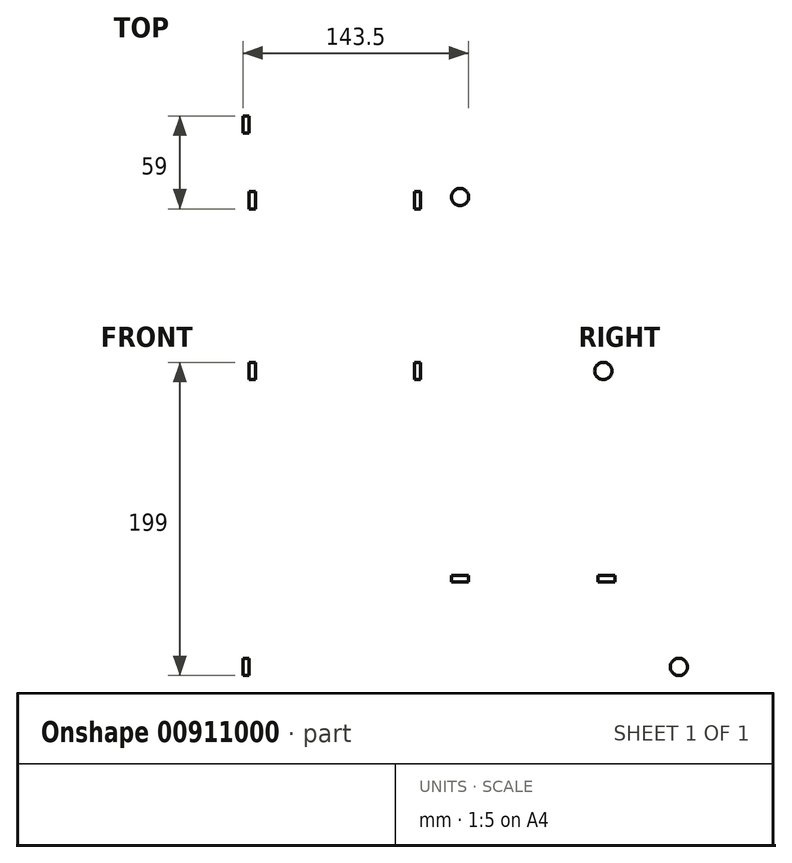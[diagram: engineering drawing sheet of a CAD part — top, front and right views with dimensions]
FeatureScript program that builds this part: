
annotation { "Feature Type Name" : "Feature", "Feature Type Description" : "" }
export const myFeature = defineFeature(function(context is Context, id is Id, definition is map)
    precondition{}
    {
        {
            var Q0;
            Q0=qCreatedBy(makeId("Front.planeOp"),FACE);
            var sketch = newSketch(context, id + "F0", { "sketchPlane" : qUnion([Q0])});
            skLineSegment(sketch, "E0", {"start": v(0, 0) * mm, "end": v(150, 0) * mm});
            skLineSegment(sketch, "E1", {"start": v(0, 0) * mm, "end": v(0, -70) * mm});
            skLineSegment(sketch, "E2.0", {"start": v(-4, 4) * mm, "end": v(-4, -70) * mm});
            skLineSegment(sketch, "E2.1", {"start": v(-4, 4) * mm, "end": v(150, 4) * mm});
            skLineSegment(sketch, "E3", {"start": v(-4, -70) * mm, "end": v(0, -70) * mm});
            skLineSegment(sketch, "E4", {"start": v(150, 0) * mm, "end": v(150, 4) * mm});
            skSolve(sketch);
        }
        {
            var Q0;
            Q0=makeQuery(id+"F0.imprint","IMPRINT",FACE,{"disambiguationData":[TD([[makeQuery(id+"F0.imprint","IMPRINT",EDGE,{"derivedFrom":sQuery(id+"F0.wireOp",EDGE,"E0")}),1.0]])]});
            var sketch = newSketch(context, id + "F1", { "sketchPlane" : qUnion([Q0])});
            skLineSegment(sketch, "E5", {"start": v(105, 4) * mm, "end": v(105, 204) * mm});
            skLineSegment(sketch, "E6", {"start": v(4, 83) * mm, "end": v(105, 83) * mm});
            skLineSegment(sketch, "E7.0", {"start": v(0, 4) * mm, "end": v(0, 204) * mm});
            skLineSegment(sketch, "E8.0", {"start": v(109, 4) * mm, "end": v(109, 204) * mm});
            skLineSegment(sketch, "E9.0", {"start": v(4, 79) * mm, "end": v(105, 79) * mm});
            skLineSegment(sketch, "E10", {"start": v(109, 4) * mm, "end": v(105, 4) * mm});
            skLineSegment(sketch, "E11", {"start": v(0, 4) * mm, "end": v(4, 4) * mm});
            skLineSegment(sketch, "E12", {"start": v(4, 4) * mm, "end": v(4, 204) * mm});
            skLineSegment(sketch, "E13", {"start": v(4, 204) * mm, "end": v(0, 204) * mm});
            skLineSegment(sketch, "E14", {"start": v(109, 204) * mm, "end": v(105, 204) * mm});
            skSolve(sketch);
        }
        {
            var Q0;
            Q0=makeQuery(id+"F0.imprint","IMPRINT",FACE,{"disambiguationData":[TD([[makeQuery(id+"F0.imprint","IMPRINT",EDGE,{"derivedFrom":sQuery(id+"F0.wireOp",EDGE,"E0")}),1.0]])]});
            var Q1;
            Q1=makeQuery(id+"F1.imprint","IMPRINT",FACE,{"disambiguationData":[TD([[makeQuery(id+"F1.imprint","IMPRINT",EDGE,{"derivedFrom":sQuery(id+"F1.wireOp",EDGE,"E7.0")}),-1.0]])]});
            var Q2;
            {var subQ0=sQuery(id+"F1.wireOp",EDGE,"E6");Q2=makeQuery(id+"F1.imprint","IMPRINT",FACE,{"disambiguationData":[TD([[makeQuery(id+"F1.imprint","IMPRINT",EDGE,{"derivedFrom":subQ0}),-1.0]])]});}
            var Q3;
            Q3=makeQuery(id+"F1.imprint","IMPRINT",FACE,{"disambiguationData":[TD([[makeQuery(id+"F1.imprint","IMPRINT",EDGE,{"derivedFrom":sQuery(id+"F1.wireOp",EDGE,"E8.0")}),1.0]])]});
            extrude(context, id + "F2", {"entities" : qUnion([Q0, Q1, Q2, Q3]), "depth" : 80 * mm, "offsetDistance" : 25 * mm});
        }
        {
            var Q0;
            Q0=makeQuery(id+"F2.opExtrude","SWEPT_FACE",FACE,{"disambiguationData":[OSD([sQuery(id+"F0.wireOp",EDGE,"E2.1")])]});
            var sketch = newSketch(context, id + "F3", { "sketchPlane" : qUnion([Q0])});
            skLineSegment(sketch, "E15", {"start": v(150, -40) * mm, "end": v(105.86, -40) * mm, "construction": true});
            skCircle(sketch, "E16", {"center": v(134, -17) * mm, "radius": 5.5 * mm});
            skCircle(sketch, "E17.MirrorC", {"center": v(134, -63) * mm, "radius": 5.5 * mm});
            skSolve(sketch);
        }
        {
            var Q0;
            Q0=makeQuery(id+"F2.opExtrude","SWEPT_FACE",FACE,{"disambiguationData":[OSD([sQuery(id+"F0.wireOp",EDGE,"E2.0")])]});
            var sketch = newSketch(context, id + "F4", { "sketchPlane" : qUnion([Q0])});
            skCircle(sketch, "E18", {"center": v(63, -54) * mm, "radius": 5.5 * mm});
            skLineSegment(sketch, "E19", {"start": v(40, -70) * mm, "end": v(40, -26.92) * mm, "construction": true});
            skCircle(sketch, "E20.MirrorC", {"center": v(17, -54) * mm, "radius": 5.5 * mm});
            skSolve(sketch);
        }
        {
            var Q0;
            Q0=makeQuery(id+"F3.imprint","IMPRINT",FACE,{"disambiguationData":[TD([[makeQuery(id+"F3.imprint","IMPRINT",EDGE,{"derivedFrom":sQuery(id+"F3.wireOp",EDGE,"E16")}),1.0]])]});
            var Q1;
            Q1=makeQuery(id+"F3.imprint","IMPRINT",FACE,{"disambiguationData":[TD([[makeQuery(id+"F3.imprint","IMPRINT",EDGE,{"derivedFrom":sQuery(id+"F3.wireOp",EDGE,"E17.MirrorC")}),-1.0]])]});
            extrude(context, id + "F5", {"entities" : qUnion([Q0, Q1]), "operationType" : NewBodyOperationType.REMOVE, "oppositeDirection" : true, "depth" : 25 * mm, "offsetDistance" : 25 * mm});
        }
        {
            var Q0;
            Q0=makeQuery(id+"F4.imprint","IMPRINT",FACE,{"disambiguationData":[TD([[makeQuery(id+"F4.imprint","IMPRINT",EDGE,{"derivedFrom":sQuery(id+"F4.wireOp",EDGE,"E20.MirrorC")}),-1.0]])]});
            var Q1;
            Q1=makeQuery(id+"F4.imprint","IMPRINT",FACE,{"disambiguationData":[TD([[makeQuery(id+"F4.imprint","IMPRINT",EDGE,{"derivedFrom":sQuery(id+"F4.wireOp",EDGE,"E18")}),1.0]])]});
            extrude(context, id + "F6", {"entities" : qUnion([Q0, Q1]), "operationType" : NewBodyOperationType.REMOVE, "oppositeDirection" : true, "depth" : 25 * mm, "offsetDistance" : 25 * mm});
        }
        {
            var Q0;
            Q0=makeQuery(id+"F2.opExtrude","SWEPT_FACE",FACE,{"disambiguationData":[OSD([sQuery(id+"F1.wireOp",EDGE,"E8.0")])]});
            var sketch = newSketch(context, id + "F7", { "sketchPlane" : qUnion([Q0])});
            skLineSegment(sketch, "E21", {"start": v(-40, 204) * mm, "end": v(-40, 86.6) * mm, "construction": true});
            skCircle(sketch, "E22", {"center": v(-15, 134) * mm, "radius": 5.5 * mm});
            skCircle(sketch, "E23", {"center": v(-40, 176) * mm, "radius": 5.5 * mm});
            skCircle(sketch, "E24.MirrorC", {"center": v(-65, 134) * mm, "radius": 5.5 * mm});
            skSolve(sketch);
        }
        {
            var Q0;
            Q0=makeQuery(id+"F7.imprint","IMPRINT",FACE,{"disambiguationData":[TD([[makeQuery(id+"F7.imprint","IMPRINT",EDGE,{"derivedFrom":sQuery(id+"F7.wireOp",EDGE,"E23")}),1.0]])]});
            var Q1;
            Q1=makeQuery(id+"F7.imprint","IMPRINT",FACE,{"disambiguationData":[TD([[makeQuery(id+"F7.imprint","IMPRINT",EDGE,{"derivedFrom":sQuery(id+"F7.wireOp",EDGE,"E22")}),1.0]])]});
            var Q2;
            Q2=makeQuery(id+"F7.imprint","IMPRINT",FACE,{"disambiguationData":[TD([[makeQuery(id+"F7.imprint","IMPRINT",EDGE,{"derivedFrom":sQuery(id+"F7.wireOp",EDGE,"E24.MirrorC")}),-1.0]])]});
            extrude(context, id + "F8", {"entities" : qUnion([Q0, Q1, Q2]), "operationType" : NewBodyOperationType.REMOVE, "endBound" : BoundingType.THROUGH_ALL, "oppositeDirection" : true, "depth" : 25 * mm, "offsetDistance" : 25 * mm});
        }
    });
